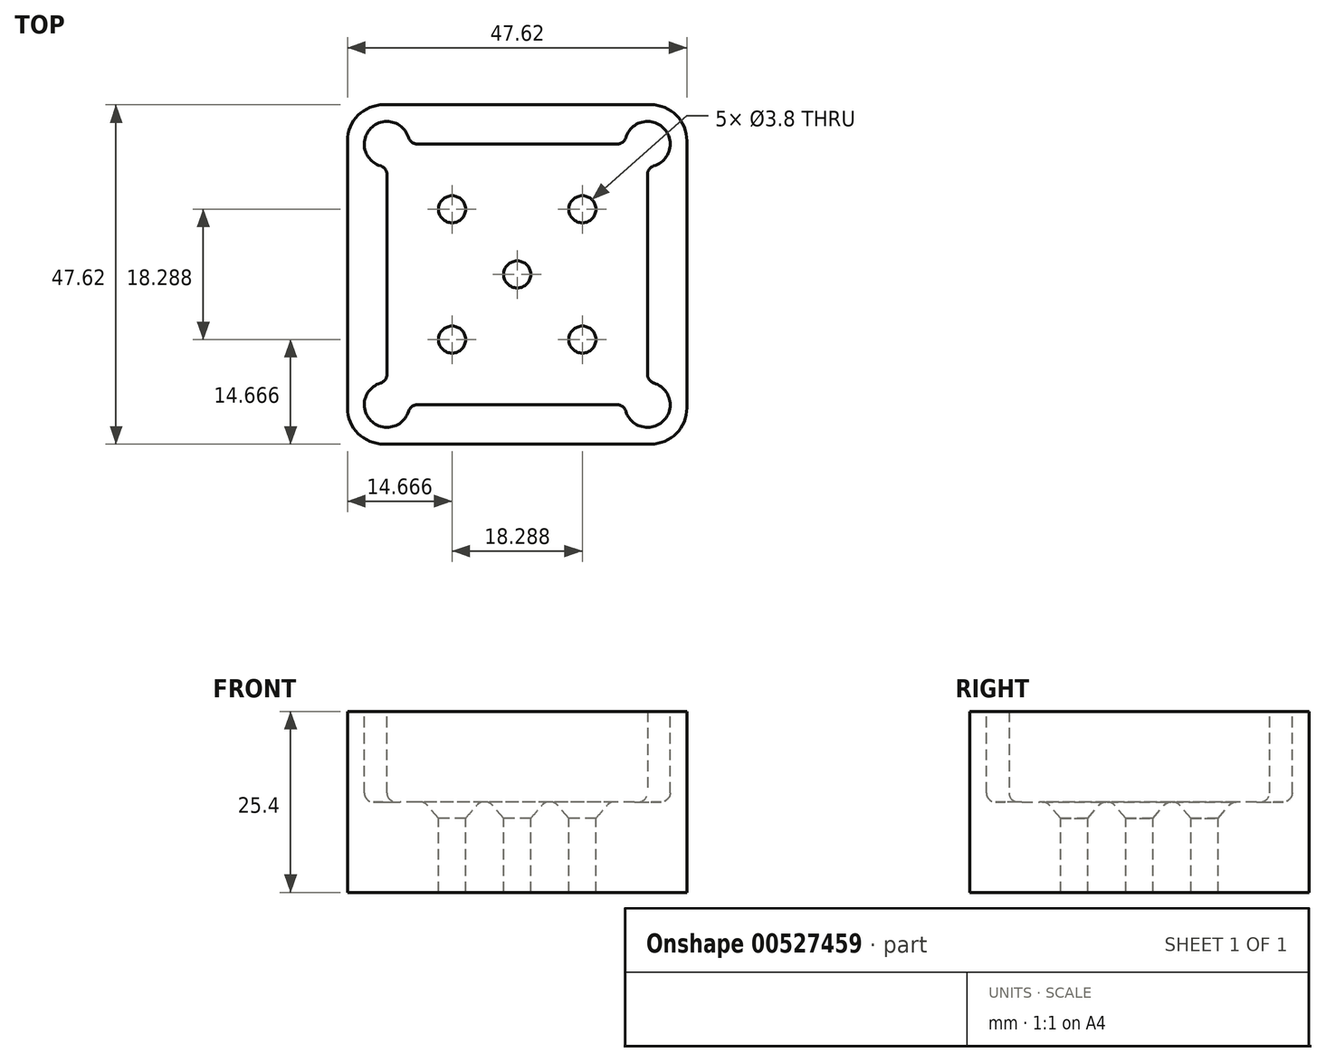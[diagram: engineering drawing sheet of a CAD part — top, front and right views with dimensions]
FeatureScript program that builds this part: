
annotation { "Feature Type Name" : "Feature", "Feature Type Description" : "" }
export const myFeature = defineFeature(function(context is Context, id is Id, definition is map)
    precondition{}
    {
        {
            var Q0;
            Q0=qCreatedBy(makeId("Top.planeOp"),FACE);
            var sketch = newSketch(context, id + "F0", { "sketchPlane" : qUnion([Q0])});
            skLineSegment(sketch, "E0.bottom", {"start": v(23.81, 23.81) * mm, "end": v(-23.81, 23.81) * mm});
            skLineSegment(sketch, "E0.top", {"start": v(23.81, -23.81) * mm, "end": v(-23.81, -23.81) * mm});
            skLineSegment(sketch, "E0.left", {"start": v(23.81, 23.81) * mm, "end": v(23.81, -23.81) * mm});
            skLineSegment(sketch, "E0.right", {"start": v(-23.81, 23.81) * mm, "end": v(-23.81, -23.81) * mm});
            skPoint(sketch, "E0.middle", {"position": v(0, 0) * mm});
            skSolve(sketch);
        }
        {
            var Q0;
            Q0=makeQuery(id+"F0.imprint","IMPRINT",FACE,{"disambiguationData":[TD([[makeQuery(id+"F0.imprint","IMPRINT",EDGE,{"derivedFrom":sQuery(id+"F0.wireOp",EDGE,"E0.bottom")}),1.0]])]});
            extrude(context, id + "F1", {"entities" : qUnion([Q0]), "depth" : 25.4 * mm, "offsetDistance" : 25.4 * mm});
        }
        {
            var Q0;
            Q0=makeQuery(id+"F1.opExtrude","CAP_FACE",FACE,{"disambiguationData":[OSD([sQuery(id+"F0.wireOp",EDGE,"E0.bottom"),sQuery(id+"F0.wireOp",EDGE,"E0.top"),sQuery(id+"F0.wireOp",EDGE,"E0.left"),sQuery(id+"F0.wireOp",EDGE,"E0.right")])],"isStart":false});
            var sketch = newSketch(context, id + "F2", { "sketchPlane" : qUnion([Q0])});
            skLineSegment(sketch, "E1.bottom", {"start": v(18.29, 18.29) * mm, "end": v(-18.29, 18.29) * mm});
            skLineSegment(sketch, "E1.top", {"start": v(18.29, -18.29) * mm, "end": v(-18.29, -18.29) * mm});
            skLineSegment(sketch, "E1.left", {"start": v(18.29, 18.29) * mm, "end": v(18.29, -18.29) * mm});
            skLineSegment(sketch, "E1.right", {"start": v(-18.29, 18.29) * mm, "end": v(-18.29, -18.29) * mm});
            skPoint(sketch, "E1.middle", {"position": v(0, 0) * mm});
            skSolve(sketch);
        }
        {
            var Q0;
            Q0=makeQuery(id+"F2.imprint","IMPRINT",FACE,{"disambiguationData":[TD([[makeQuery(id+"F2.imprint","IMPRINT",EDGE,{"derivedFrom":sQuery(id+"F2.wireOp",EDGE,"E1.bottom")}),1.0]])]});
            extrude(context, id + "F3", {"entities" : qUnion([Q0]), "operationType" : NewBodyOperationType.REMOVE, "oppositeDirection" : true, "depth" : 12.7 * mm, "offsetDistance" : 25.4 * mm});
        }
        {
            var Q0;
            Q0=makeQuery(id+"F1.opExtrude","SWEPT_EDGE",EDGE,{"disambiguationData":[OSD([sQuery(id+"F0.wireOp",EDGE,"E0.top"),sQuery(id+"F0.wireOp",EDGE,"E0.right")])]});
            var Q1;
            Q1=makeQuery(id+"F1.opExtrude","SWEPT_EDGE",EDGE,{"disambiguationData":[OSD([sQuery(id+"F0.wireOp",EDGE,"E0.top"),sQuery(id+"F0.wireOp",EDGE,"E0.left")])]});
            var Q2;
            Q2=makeQuery(id+"F1.opExtrude","SWEPT_EDGE",EDGE,{"disambiguationData":[OSD([sQuery(id+"F0.wireOp",EDGE,"E0.bottom"),sQuery(id+"F0.wireOp",EDGE,"E0.right")])]});
            var Q3;
            Q3=makeQuery(id+"F1.opExtrude","SWEPT_EDGE",EDGE,{"disambiguationData":[OSD([sQuery(id+"F0.wireOp",EDGE,"E0.bottom"),sQuery(id+"F0.wireOp",EDGE,"E0.left")])]});
            fillet(context, id + "F4", {"entities" : qUnion([Q0, Q1, Q2, Q3]), "radius" : 5.08 * mm, "tangentPropagation" : true, "allowEdgeOverflow" : false});
        }
        {
            var Q0;
            Q0=makeQuery(id+"F1.opExtrude","CAP_FACE",FACE,{"disambiguationData":[OSD([sQuery(id+"F0.wireOp",EDGE,"E0.bottom"),sQuery(id+"F0.wireOp",EDGE,"E0.top"),sQuery(id+"F0.wireOp",EDGE,"E0.left"),sQuery(id+"F0.wireOp",EDGE,"E0.right")])],"isStart":false});
            var sketch = newSketch(context, id + "F5", { "sketchPlane" : qUnion([Q0])});
            skCircle(sketch, "E2", {"center": v(-18.29, 18.29) * mm, "radius": 3.18 * mm});
            skCircle(sketch, "E3", {"center": v(18.29, 18.29) * mm, "radius": 3.18 * mm});
            skCircle(sketch, "E4", {"center": v(18.29, -18.29) * mm, "radius": 3.18 * mm});
            skCircle(sketch, "E5", {"center": v(-18.29, -18.29) * mm, "radius": 3.18 * mm});
            skSolve(sketch);
        }
        {
            var Q0;
            {var subQ0=sQuery(id+"F5.wireOp",EDGE,"E2");var subQ1=makeQuery(id+"F3.boolean.opBoolean","COPY",EDGE,{"derivedFrom":makeQuery(id+"F3.opExtrude","CAP_EDGE",EDGE,{"disambiguationData":[OSD([sQuery(id+"F2.wireOp",EDGE,"E1.bottom")])],"isStart":true})});var subQ2=makeQuery(id+"F5.imprint","INTERSECT",VERTEX,{"derivedFrom":[subQ1,subQ0]});Q0=makeQuery(id+"F5.imprint","IMPRINT",FACE,{"disambiguationData":[TD([[makeQuery(id+"F5.imprint","IMPRINT",EDGE,{"disambiguationData":[TD([[subQ2,-1.0]])],"derivedFrom":subQ0}),1.0]])]});}
            var Q1;
            {var subQ0=sQuery(id+"F5.wireOp",EDGE,"E2");var subQ1=makeQuery(id+"F3.boolean.opBoolean","COPY",EDGE,{"derivedFrom":makeQuery(id+"F3.opExtrude","CAP_EDGE",EDGE,{"disambiguationData":[OSD([sQuery(id+"F2.wireOp",EDGE,"E1.bottom")])],"isStart":true})});var subQ2=makeQuery(id+"F5.imprint","INTERSECT",VERTEX,{"derivedFrom":[subQ1,subQ0]});Q1=makeQuery(id+"F5.imprint","IMPRINT",FACE,{"disambiguationData":[TD([[makeQuery(id+"F5.imprint","IMPRINT",EDGE,{"disambiguationData":[TD([[subQ2,1.0]])],"derivedFrom":subQ0}),1.0]])]});}
            var Q2;
            {var subQ0=sQuery(id+"F5.wireOp",EDGE,"E3");var subQ1=makeQuery(id+"F3.boolean.opBoolean","COPY",EDGE,{"derivedFrom":makeQuery(id+"F3.opExtrude","CAP_EDGE",EDGE,{"disambiguationData":[OSD([sQuery(id+"F2.wireOp",EDGE,"E1.bottom")])],"isStart":true})});var subQ2=makeQuery(id+"F5.imprint","INTERSECT",VERTEX,{"derivedFrom":[subQ1,subQ0]});Q2=makeQuery(id+"F5.imprint","IMPRINT",FACE,{"disambiguationData":[TD([[makeQuery(id+"F5.imprint","IMPRINT",EDGE,{"disambiguationData":[TD([[subQ2,1.0]])],"derivedFrom":subQ0}),1.0]])]});}
            var Q3;
            {var subQ0=sQuery(id+"F5.wireOp",EDGE,"E3");var subQ1=makeQuery(id+"F3.boolean.opBoolean","COPY",EDGE,{"derivedFrom":makeQuery(id+"F3.opExtrude","CAP_EDGE",EDGE,{"disambiguationData":[OSD([sQuery(id+"F2.wireOp",EDGE,"E1.bottom")])],"isStart":true})});var subQ2=makeQuery(id+"F5.imprint","INTERSECT",VERTEX,{"derivedFrom":[subQ1,subQ0]});Q3=makeQuery(id+"F5.imprint","IMPRINT",FACE,{"disambiguationData":[TD([[makeQuery(id+"F5.imprint","IMPRINT",EDGE,{"disambiguationData":[TD([[subQ2,-1.0]])],"derivedFrom":subQ0}),1.0]])]});}
            var Q4;
            {var subQ0=sQuery(id+"F5.wireOp",EDGE,"E5");var subQ1=makeQuery(id+"F3.boolean.opBoolean","COPY",EDGE,{"derivedFrom":makeQuery(id+"F3.opExtrude","CAP_EDGE",EDGE,{"disambiguationData":[OSD([sQuery(id+"F2.wireOp",EDGE,"E1.top")])],"isStart":true})});var subQ2=makeQuery(id+"F5.imprint","INTERSECT",VERTEX,{"derivedFrom":[subQ1,subQ0]});Q4=makeQuery(id+"F5.imprint","IMPRINT",FACE,{"disambiguationData":[TD([[makeQuery(id+"F5.imprint","IMPRINT",EDGE,{"disambiguationData":[TD([[subQ2,-1.0]])],"derivedFrom":subQ0}),1.0]])]});}
            var Q5;
            {var subQ0=sQuery(id+"F5.wireOp",EDGE,"E5");var subQ1=makeQuery(id+"F3.boolean.opBoolean","COPY",EDGE,{"derivedFrom":makeQuery(id+"F3.opExtrude","CAP_EDGE",EDGE,{"disambiguationData":[OSD([sQuery(id+"F2.wireOp",EDGE,"E1.top")])],"isStart":true})});var subQ2=makeQuery(id+"F5.imprint","INTERSECT",VERTEX,{"derivedFrom":[subQ1,subQ0]});Q5=makeQuery(id+"F5.imprint","IMPRINT",FACE,{"disambiguationData":[TD([[makeQuery(id+"F5.imprint","IMPRINT",EDGE,{"disambiguationData":[TD([[subQ2,1.0]])],"derivedFrom":subQ0}),1.0]])]});}
            var Q6;
            {var subQ0=sQuery(id+"F5.wireOp",EDGE,"E4");var subQ1=makeQuery(id+"F3.boolean.opBoolean","COPY",EDGE,{"derivedFrom":makeQuery(id+"F3.opExtrude","CAP_EDGE",EDGE,{"disambiguationData":[OSD([sQuery(id+"F2.wireOp",EDGE,"E1.top")])],"isStart":true})});var subQ2=makeQuery(id+"F5.imprint","INTERSECT",VERTEX,{"derivedFrom":[subQ1,subQ0]});Q6=makeQuery(id+"F5.imprint","IMPRINT",FACE,{"disambiguationData":[TD([[makeQuery(id+"F5.imprint","IMPRINT",EDGE,{"disambiguationData":[TD([[subQ2,-1.0]])],"derivedFrom":subQ0}),1.0]])]});}
            var Q7;
            {var subQ0=sQuery(id+"F5.wireOp",EDGE,"E4");var subQ1=makeQuery(id+"F3.boolean.opBoolean","COPY",EDGE,{"derivedFrom":makeQuery(id+"F3.opExtrude","CAP_EDGE",EDGE,{"disambiguationData":[OSD([sQuery(id+"F2.wireOp",EDGE,"E1.top")])],"isStart":true})});var subQ2=makeQuery(id+"F5.imprint","INTERSECT",VERTEX,{"derivedFrom":[subQ1,subQ0]});Q7=makeQuery(id+"F5.imprint","IMPRINT",FACE,{"disambiguationData":[TD([[makeQuery(id+"F5.imprint","IMPRINT",EDGE,{"disambiguationData":[TD([[subQ2,1.0]])],"derivedFrom":subQ0}),1.0]])]});}
            var Q8;
            Q8=makeQuery(id+"F3.boolean.opBoolean","COPY",FACE,{"derivedFrom":makeQuery(id+"F3.opExtrude","CAP_FACE",FACE,{"disambiguationData":[OSD([sQuery(id+"F2.wireOp",EDGE,"E1.bottom"),sQuery(id+"F2.wireOp",EDGE,"E1.top"),sQuery(id+"F2.wireOp",EDGE,"E1.left"),sQuery(id+"F2.wireOp",EDGE,"E1.right")])],"isStart":false})});
            extrude(context, id + "F6", {"entities" : qUnion([Q0, Q1, Q2, Q3, Q4, Q5, Q6, Q7]), "operationType" : NewBodyOperationType.REMOVE, "endBound" : BoundingType.UP_TO_SURFACE, "oppositeDirection" : true, "depth" : 25.4 * mm, "endBoundEntityFace" : qUnion([Q8]), "offsetDistance" : 25.4 * mm});
        }
        {
            var Q0;
            {var subQ0=sQuery(id+"F2.wireOp",EDGE,"E1.right");var subQ1=sQuery(id+"F2.wireOp",EDGE,"E1.left");var subQ2=sQuery(id+"F2.wireOp",EDGE,"E1.top");var subQ3=sQuery(id+"F2.wireOp",EDGE,"E1.bottom");Q0=makeQuery(id+"F6.boolean.opBoolean","MERGE",FACE,{"derivedFrom":[makeQuery(id+"F3.boolean.opBoolean","COPY",FACE,{"derivedFrom":makeQuery(id+"F3.opExtrude","CAP_FACE",FACE,{"disambiguationData":[OSD([subQ3,subQ2,subQ1,subQ0])],"isStart":false})}),makeQuery(id+"F6.opExtrude","CAP_FACE",FACE,{"disambiguationData":[OSD([subQ3,subQ2,subQ1,subQ0]),OD(0.0)],"isStart":false}),makeQuery(id+"F6.opExtrude","CAP_FACE",FACE,{"disambiguationData":[OSD([subQ3,subQ2,subQ1,subQ0]),OD(1.0)],"isStart":false}),makeQuery(id+"F6.opExtrude","CAP_FACE",FACE,{"disambiguationData":[OSD([subQ3,subQ2,subQ1,subQ0]),OD(2.0)],"isStart":false}),makeQuery(id+"F6.opExtrude","CAP_FACE",FACE,{"disambiguationData":[OSD([subQ3,subQ2,subQ1,subQ0]),OD(3.0)],"isStart":false})]});}
            var sketch = newSketch(context, id + "F7", { "sketchPlane" : qUnion([Q0])});
            skLineSegment(sketch, "E6", {"start": v(0, 0) * mm, "end": v(-18.29, -18.29) * mm});
            skLineSegment(sketch, "E7", {"start": v(0, 0) * mm, "end": v(18.29, 18.29) * mm});
            skPoint(sketch, "E8", {"position": v(-9.14, -9.14) * mm});
            skPoint(sketch, "E9", {"position": v(9.14, 9.14) * mm});
            skLineSegment(sketch, "E10", {"start": v(0, 0) * mm, "end": v(-18.29, 18.29) * mm});
            skLineSegment(sketch, "E11", {"start": v(18.29, -18.29) * mm, "end": v(0, 0) * mm});
            skPoint(sketch, "E12", {"position": v(-9.14, 9.14) * mm});
            skPoint(sketch, "E13", {"position": v(9.14, -9.14) * mm});
            skSolve(sketch);
        }
        {
            var Q0;
            Q0=sQuery(id+"F7.wireOp",VERTEX,"E8");
            var Q1;
            Q1=sQuery(id+"F7.wireOp",VERTEX,"E9");
            var Q2;
            Q2=sQuery(id+"F7.wireOp",VERTEX,"E6.start");
            var Q3;
            Q3=sQuery(id+"F7.wireOp",VERTEX,"E12");
            var Q4;
            Q4=sQuery(id+"F7.wireOp",VERTEX,"E13");
            var Q5;
            Q5=makeQuery(id+"F1.opExtrude","SWEPT_BODY",BODY,{"disambiguationData":[OSD([sQuery(id+"F0.wireOp",EDGE,"E0.bottom"),sQuery(id+"F0.wireOp",EDGE,"E0.top"),sQuery(id+"F0.wireOp",EDGE,"E0.left"),sQuery(id+"F0.wireOp",EDGE,"E0.right")])]});
            hole(context, id + "F8", {"style" : HoleStyle.C_SINK, "endStyle" : HoleEndStyle.THROUGH, "standardTappedOrClearance" : lookupTablePath({ "standard" : "ANSI", "fit" : "Normal (ASME)", "size" : "#6", "type" : "Clearance" }), "standardBlindInLast" : lookupTablePath({ "fit" : "Free", "standard" : "ANSI", "size" : "#6", "type" : "Clearance" }), "holeDiameter" : 3.8 * mm, "cSinkDiameter" : 7.8 * mm, "cSinkAngle" : 82 * degree, "majorDiameter" : 6.35 * mm, "isTappedThrough" : true, "tappedDepth" : 12.7 * mm, "tapClearance" : 3, "locations" : qUnion([Q0, Q1, Q2, Q3, Q4]), "scope" : qUnion([Q5])});
        }
        {
            var Q0;
            {var subQ0=sQuery(id+"F5.wireOp",EDGE,"E2");var subQ1=sQuery(id+"F2.wireOp",EDGE,"E1.bottom");var subQ2=makeQuery(id+"F5.imprint","INTERSECT",VERTEX,{"derivedFrom":[makeQuery(id+"F3.boolean.opBoolean","COPY",EDGE,{"derivedFrom":makeQuery(id+"F3.opExtrude","CAP_EDGE",EDGE,{"disambiguationData":[OSD([subQ1])],"isStart":true})}),subQ0]});var subQ3=sQuery(id+"F2.wireOp",EDGE,"E1.right");Q0=makeQuery(id+"F6.boolean.opBoolean","COPY",EDGE,{"derivedFrom":makeQuery(id+"F6.opExtrude","TWEAK_EDGE",EDGE,{"derivedFrom":[makeQuery(id+"F3.boolean.opBoolean","COPY",FACE,{"derivedFrom":makeQuery(id+"F3.opExtrude","CAP_FACE",FACE,{"disambiguationData":[OSD([subQ1,sQuery(id+"F2.wireOp",EDGE,"E1.top"),sQuery(id+"F2.wireOp",EDGE,"E1.left"),subQ3])],"isStart":false})}),makeQuery(id+"F5.imprint","IMPRINT",EDGE,{"disambiguationData":[TD([[subQ2,-1.0]])],"derivedFrom":subQ0}),makeQuery(id+"F5.imprint","IMPRINT",EDGE,{"disambiguationData":[TD([[subQ2,1.0]])],"derivedFrom":subQ0})]})});}
            var Q1;
            Q1=makeQuery(id+"F3.boolean.opBoolean","COPY",EDGE,{"derivedFrom":makeQuery(id+"F3.opExtrude","CAP_EDGE",EDGE,{"disambiguationData":[OSD([sQuery(id+"F2.wireOp",EDGE,"E1.bottom")])],"isStart":false})});
            var Q2;
            {var subQ0=sQuery(id+"F5.wireOp",EDGE,"E3");var subQ1=sQuery(id+"F2.wireOp",EDGE,"E1.bottom");var subQ2=makeQuery(id+"F5.imprint","INTERSECT",VERTEX,{"derivedFrom":[makeQuery(id+"F3.boolean.opBoolean","COPY",EDGE,{"derivedFrom":makeQuery(id+"F3.opExtrude","CAP_EDGE",EDGE,{"disambiguationData":[OSD([subQ1])],"isStart":true})}),subQ0]});var subQ3=sQuery(id+"F2.wireOp",EDGE,"E1.left");Q2=makeQuery(id+"F6.boolean.opBoolean","COPY",EDGE,{"derivedFrom":makeQuery(id+"F6.opExtrude","TWEAK_EDGE",EDGE,{"derivedFrom":[makeQuery(id+"F3.boolean.opBoolean","COPY",FACE,{"derivedFrom":makeQuery(id+"F3.opExtrude","CAP_FACE",FACE,{"disambiguationData":[OSD([subQ1,sQuery(id+"F2.wireOp",EDGE,"E1.top"),subQ3,sQuery(id+"F2.wireOp",EDGE,"E1.right")])],"isStart":false})}),makeQuery(id+"F5.imprint","IMPRINT",EDGE,{"disambiguationData":[TD([[subQ2,-1.0]])],"derivedFrom":subQ0}),makeQuery(id+"F5.imprint","IMPRINT",EDGE,{"disambiguationData":[TD([[subQ2,1.0]])],"derivedFrom":subQ0})]})});}
            var Q3;
            Q3=makeQuery(id+"F3.boolean.opBoolean","COPY",EDGE,{"derivedFrom":makeQuery(id+"F3.opExtrude","CAP_EDGE",EDGE,{"disambiguationData":[OSD([sQuery(id+"F2.wireOp",EDGE,"E1.left")])],"isStart":false})});
            var Q4;
            {var subQ0=sQuery(id+"F2.wireOp",EDGE,"E1.right");var subQ1=sQuery(id+"F2.wireOp",EDGE,"E1.left");var subQ2=sQuery(id+"F2.wireOp",EDGE,"E1.top");var subQ3=sQuery(id+"F2.wireOp",EDGE,"E1.bottom");Q4=makeQuery(id+"F6.boolean.opBoolean","MERGE",FACE,{"derivedFrom":[makeQuery(id+"F3.boolean.opBoolean","COPY",FACE,{"derivedFrom":makeQuery(id+"F3.opExtrude","CAP_FACE",FACE,{"disambiguationData":[OSD([subQ3,subQ2,subQ1,subQ0])],"isStart":false})}),makeQuery(id+"F6.opExtrude","CAP_FACE",FACE,{"disambiguationData":[OSD([subQ3,subQ2,subQ1,subQ0]),OD(0.0)],"isStart":false}),makeQuery(id+"F6.opExtrude","CAP_FACE",FACE,{"disambiguationData":[OSD([subQ3,subQ2,subQ1,subQ0]),OD(1.0)],"isStart":false}),makeQuery(id+"F6.opExtrude","CAP_FACE",FACE,{"disambiguationData":[OSD([subQ3,subQ2,subQ1,subQ0]),OD(2.0)],"isStart":false}),makeQuery(id+"F6.opExtrude","CAP_FACE",FACE,{"disambiguationData":[OSD([subQ3,subQ2,subQ1,subQ0]),OD(3.0)],"isStart":false})]});}
            var Q5;
            Q5=makeQuery(id+"F6.boolean.opBoolean","INTERSECT",EDGE,{"derivedFrom":[makeQuery(id+"F3.boolean.opBoolean","COPY",FACE,{"derivedFrom":makeQuery(id+"F3.opExtrude","SWEPT_FACE",FACE,{"disambiguationData":[OSD([sQuery(id+"F2.wireOp",EDGE,"E1.right")])]})}),makeQuery(id+"F6.opExtrude","SWEPT_FACE",FACE,{"disambiguationData":[OSD([sQuery(id+"F5.wireOp",EDGE,"E5")])]})]});
            var Q6;
            Q6=makeQuery(id+"F6.boolean.opBoolean","INTERSECT",EDGE,{"derivedFrom":[makeQuery(id+"F3.boolean.opBoolean","COPY",FACE,{"derivedFrom":makeQuery(id+"F3.opExtrude","SWEPT_FACE",FACE,{"disambiguationData":[OSD([sQuery(id+"F2.wireOp",EDGE,"E1.right")])]})}),makeQuery(id+"F6.opExtrude","SWEPT_FACE",FACE,{"disambiguationData":[OSD([sQuery(id+"F5.wireOp",EDGE,"E2")])]})]});
            var Q7;
            Q7=makeQuery(id+"F6.boolean.opBoolean","INTERSECT",EDGE,{"derivedFrom":[makeQuery(id+"F3.boolean.opBoolean","COPY",FACE,{"derivedFrom":makeQuery(id+"F3.opExtrude","SWEPT_FACE",FACE,{"disambiguationData":[OSD([sQuery(id+"F2.wireOp",EDGE,"E1.top")])]})}),makeQuery(id+"F6.opExtrude","SWEPT_FACE",FACE,{"disambiguationData":[OSD([sQuery(id+"F5.wireOp",EDGE,"E5")])]})]});
            var Q8;
            Q8=makeQuery(id+"F6.boolean.opBoolean","INTERSECT",EDGE,{"derivedFrom":[makeQuery(id+"F3.boolean.opBoolean","COPY",FACE,{"derivedFrom":makeQuery(id+"F3.opExtrude","SWEPT_FACE",FACE,{"disambiguationData":[OSD([sQuery(id+"F2.wireOp",EDGE,"E1.top")])]})}),makeQuery(id+"F6.opExtrude","SWEPT_FACE",FACE,{"disambiguationData":[OSD([sQuery(id+"F5.wireOp",EDGE,"E4")])]})]});
            var Q9;
            Q9=makeQuery(id+"F6.boolean.opBoolean","INTERSECT",EDGE,{"derivedFrom":[makeQuery(id+"F3.boolean.opBoolean","COPY",FACE,{"derivedFrom":makeQuery(id+"F3.opExtrude","SWEPT_FACE",FACE,{"disambiguationData":[OSD([sQuery(id+"F2.wireOp",EDGE,"E1.bottom")])]})}),makeQuery(id+"F6.opExtrude","SWEPT_FACE",FACE,{"disambiguationData":[OSD([sQuery(id+"F5.wireOp",EDGE,"E2")])]})]});
            var Q10;
            Q10=makeQuery(id+"F6.boolean.opBoolean","INTERSECT",EDGE,{"derivedFrom":[makeQuery(id+"F3.boolean.opBoolean","COPY",FACE,{"derivedFrom":makeQuery(id+"F3.opExtrude","SWEPT_FACE",FACE,{"disambiguationData":[OSD([sQuery(id+"F2.wireOp",EDGE,"E1.bottom")])]})}),makeQuery(id+"F6.opExtrude","SWEPT_FACE",FACE,{"disambiguationData":[OSD([sQuery(id+"F5.wireOp",EDGE,"E3")])]})]});
            var Q11;
            Q11=makeQuery(id+"F6.boolean.opBoolean","INTERSECT",EDGE,{"derivedFrom":[makeQuery(id+"F3.boolean.opBoolean","COPY",FACE,{"derivedFrom":makeQuery(id+"F3.opExtrude","SWEPT_FACE",FACE,{"disambiguationData":[OSD([sQuery(id+"F2.wireOp",EDGE,"E1.left")])]})}),makeQuery(id+"F6.opExtrude","SWEPT_FACE",FACE,{"disambiguationData":[OSD([sQuery(id+"F5.wireOp",EDGE,"E3")])]})]});
            var Q12;
            Q12=makeQuery(id+"F6.boolean.opBoolean","INTERSECT",EDGE,{"derivedFrom":[makeQuery(id+"F3.boolean.opBoolean","COPY",FACE,{"derivedFrom":makeQuery(id+"F3.opExtrude","SWEPT_FACE",FACE,{"disambiguationData":[OSD([sQuery(id+"F2.wireOp",EDGE,"E1.left")])]})}),makeQuery(id+"F6.opExtrude","SWEPT_FACE",FACE,{"disambiguationData":[OSD([sQuery(id+"F5.wireOp",EDGE,"E4")])]})]});
            fillet(context, id + "F9", {"entities" : qUnion([Q0, Q1, Q2, Q3, Q4, Q5, Q6, Q7, Q8, Q9, Q10, Q11, Q12]), "radius" : 1.27 * mm, "tangentPropagation" : true, "allowEdgeOverflow" : false});
        }
    });
